# Revit family: Boiler-Weil-McLain-Evergreen_Gas_Boiler
name_source: partatom
category: Mechanical Equipment
revit_build: Autodesk Revit Architecture 2014 (Build: 20131024_2115(x64)
units: mm (PartAtom-declared; Revit-internal decimal feet)

## types (4) — shared parameters
Air Vent Radius = 2"
Back Casing = Metal - Weil-Mclain - Paint Black
Boiler Water In = 2"
Boiler Water In Radius = 1"
Boiler Water Out = 2"
Boiler Water Out Radius = 1"
Clearance Depth = 1' - 0"
Depth = 0' - 11"
Description = Evergreen High-Efficiency Condensing Gas Boiler
Feet = Plastic - Weil-Mclain - Plastic - White
Frequency = 60 Hz
Front Casing = Plastic - Weil-McLain - Paint Tan
Gas Connection Radius = 0"
Gas Connection Size = 1"
Height = 3' - 8 1/4"
Manufacturer = Weil-McLain
Manufacturer Fax = 630-560-3769
Phase = 1
Product Documentation Link = http://www.weil-mclain.com
Product Name = Evergreen Gas Boiler
Product Page URL = http://www.weil-mclain.com
URL = http://www.weil-mclain.com
Voltage = 120 V
Warranty = http://www.weil-mclain.com
Width = 1' - 11"

## per-type parameters (varying)
| type | Model |
| EVG 220 Combustion Air Size 3" | Evergreen 220 Gas Boiler |
| EVG 220 Combustion Air Size 4" | Evergreen 220 Gas Boiler |
| EVG 299 | Evergreen 299 Gas Boiler |
| EVG 399 | Evergreen 399 Gas Boiler |

## geometry (parser evidence)
native form markers: Blend x26, Sweep x12
no freeform markers — native parametric forms only
